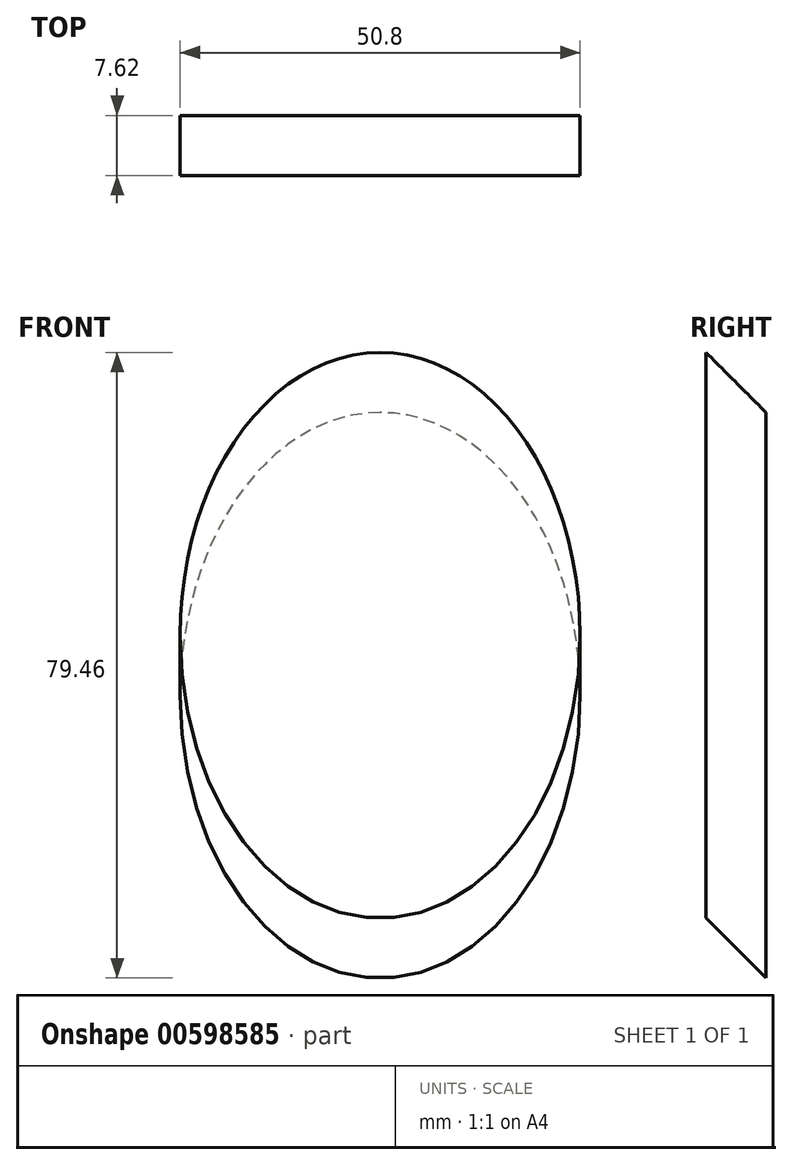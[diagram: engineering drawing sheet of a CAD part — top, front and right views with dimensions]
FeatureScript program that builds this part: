
annotation { "Feature Type Name" : "Feature", "Feature Type Description" : "" }
export const myFeature = defineFeature(function(context is Context, id is Id, definition is map)
    precondition{}
    {
        {
            var Q0;
            Q0=qCreatedBy(makeId("Front.planeOp"),FACE);
            var sketch = newSketch(context, id + "F0", { "sketchPlane" : qUnion([Q0])});
            skCircle(sketch, "E0", {"center": v(0, 0) * mm, "radius": 25.4 * mm});
            skSolve(sketch);
        }
        {
            var Q0;
            Q0=qCreatedBy(makeId("Right.planeOp"),FACE);
            var sketch = newSketch(context, id + "F1", { "sketchPlane" : qUnion([Q0])});
            skLineSegment(sketch, "E1", {"start": v(0, 0) * mm, "end": v(-7.62, 7.62) * mm});
            skSolve(sketch);
        }
        {
            var Q0;
            Q0=qCreatedBy(makeId("Front.planeOp"),FACE);
            var sketch = newSketch(context, id + "F2", { "sketchPlane" : qUnion([Q0])});
            skEllipse(sketch, "E2", {"center": v(0, 0) * mm, "majorRadius": 35.92 * mm, "minorRadius": 25.4 * mm, "majorAxis": v(0, 1)});
            skSolve(sketch);
        }
        {
            var Q0;
            Q0 = qSketchRegion(id + "F2", true);
            var Q1;
            Q1=sQuery(id+"F1.wireOp",EDGE,"E1");
            sweep(context, id + "F3", {"profiles" : qUnion([Q0]), "path" : qUnion([Q1])});
        }
    });
